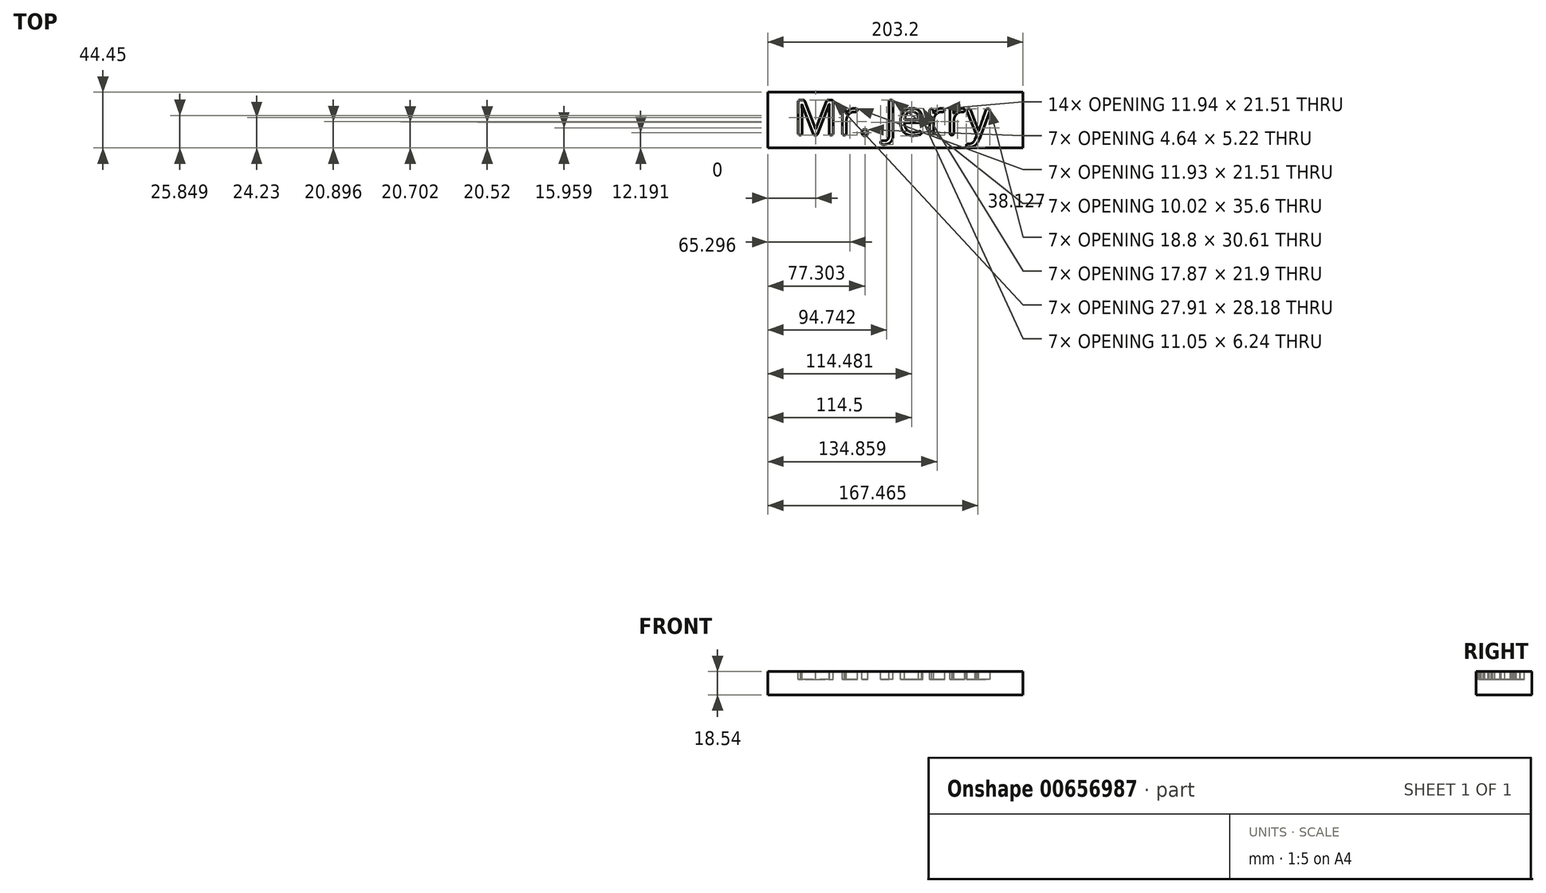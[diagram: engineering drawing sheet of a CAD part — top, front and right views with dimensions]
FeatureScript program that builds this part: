
annotation { "Feature Type Name" : "Feature", "Feature Type Description" : "" }
export const myFeature = defineFeature(function(context is Context, id is Id, definition is map)
    precondition{}
    {
        {
            var Q0;
            Q0=qCreatedBy(makeId("Top.planeOp"),FACE);
            var sketch = newSketch(context, id + "F0", { "sketchPlane" : qUnion([Q0])});
            skLineSegment(sketch, "E0.bottom", {"start": v(0, 0) * mm, "end": v(203.2, 0) * mm});
            skLineSegment(sketch, "E0.top", {"start": v(0, 44.45) * mm, "end": v(203.2, 44.45) * mm});
            skLineSegment(sketch, "E0.left", {"start": v(0, 0) * mm, "end": v(0, 44.45) * mm});
            skLineSegment(sketch, "E0.right", {"start": v(203.2, 0) * mm, "end": v(203.2, 44.45) * mm});
            skSolve(sketch);
        }
        {
            var Q0;
            Q0=makeQuery(id+"F0.imprint","IMPRINT",FACE,{"disambiguationData":[TD([[makeQuery(id+"F0.imprint","IMPRINT",EDGE,{"derivedFrom":sQuery(id+"F0.wireOp",EDGE,"E0.bottom")}),1.0]])]});
            extrude(context, id + "F1", {"entities" : qUnion([Q0]), "depth" : 18.54 * mm, "offsetDistance" : 25.4 * mm});
        }
        {
            var Q0;
            Q0=makeQuery(id+"F1.opExtrude","CAP_FACE",FACE,{"disambiguationData":[OSD([sQuery(id+"F0.wireOp",EDGE,"E0.bottom"),sQuery(id+"F0.wireOp",EDGE,"E0.top"),sQuery(id+"F0.wireOp",EDGE,"E0.left"),sQuery(id+"F0.wireOp",EDGE,"E0.right")])],"isStart":false});
            var sketch = newSketch(context, id + "F2", { "sketchPlane" : qUnion([Q0])});
            skText(sketch, "E1", { "text": "Mr. Jerry", "fontName": "OpenSans-Regular.ttf"});
            const initialGuessF2  = {"E1": [0.0203, 0.01014, 1, 0, 0.02842]};
            skSetInitialGuess(sketch, initialGuessF2);
            skSolve(sketch);
        }
        {
            var Q0;
            Q0 = qSketchRegion(id + "F2", true);
            extrude(context, id + "F3", {"entities" : qUnion([Q0]), "operationType" : NewBodyOperationType.REMOVE, "oppositeDirection" : true, "depth" : 6.35 * mm, "offsetDistance" : 25.4 * mm});
        }
        {
            var Q0;
            Q0=makeQuery(id+"F3.boolean.opBoolean","COPY",EDGE,{"derivedFrom":makeQuery(id+"F3.opExtrude","SWEPT_EDGE",EDGE,{"disambiguationData":[OSD([sQuery(id+"F2.wireOp",EDGE,"E1.sketch_text.stroke-5"),sQuery(id+"F2.wireOp",EDGE,"E1.sketch_text.stroke-6")])]})});
            var Q1;
            Q1=makeQuery(id+"F3.boolean.opBoolean","COPY",EDGE,{"derivedFrom":makeQuery(id+"F3.opExtrude","SWEPT_EDGE",EDGE,{"disambiguationData":[OSD([sQuery(id+"F2.wireOp",EDGE,"E1.sketch_text.stroke-6"),sQuery(id+"F2.wireOp",EDGE,"E1.sketch_text.stroke-7")])]})});
            var Q2;
            Q2=makeQuery(id+"F3.boolean.opBoolean","COPY",EDGE,{"derivedFrom":makeQuery(id+"F3.opExtrude","SWEPT_EDGE",EDGE,{"disambiguationData":[OSD([sQuery(id+"F2.wireOp",EDGE,"E1.sketch_text.stroke-9"),sQuery(id+"F2.wireOp",EDGE,"E1.sketch_text.stroke-10")])]})});
            var Q3;
            Q3=makeQuery(id+"F3.boolean.opBoolean","COPY",EDGE,{"derivedFrom":makeQuery(id+"F3.opExtrude","SWEPT_EDGE",EDGE,{"disambiguationData":[OSD([sQuery(id+"F2.wireOp",EDGE,"E1.sketch_text.stroke-10"),sQuery(id+"F2.wireOp",EDGE,"E1.sketch_text.stroke-11")])]})});
            var Q4;
            Q4=makeQuery(id+"F3.boolean.opBoolean","COPY",EDGE,{"derivedFrom":makeQuery(id+"F3.opExtrude","SWEPT_EDGE",EDGE,{"disambiguationData":[OSD([sQuery(id+"F2.wireOp",EDGE,"E1.sketch_text.stroke-26"),sQuery(id+"F2.wireOp",EDGE,"E1.sketch_text.stroke-27")])]})});
            var Q5;
            Q5=makeQuery(id+"F3.boolean.opBoolean","COPY",EDGE,{"derivedFrom":makeQuery(id+"F3.opExtrude","SWEPT_EDGE",EDGE,{"disambiguationData":[OSD([sQuery(id+"F2.wireOp",EDGE,"E1.sketch_text.stroke-18"),sQuery(id+"F2.wireOp",EDGE,"E1.sketch_text.stroke-19")])]})});
            var Q6;
            Q6=makeQuery(id+"F3.boolean.opBoolean","COPY",EDGE,{"derivedFrom":makeQuery(id+"F3.opExtrude","SWEPT_EDGE",EDGE,{"disambiguationData":[OSD([sQuery(id+"F2.wireOp",EDGE,"E1.sketch_text.stroke-25"),sQuery(id+"F2.wireOp",EDGE,"E1.sketch_text.stroke-26")])]})});
            var Q7;
            Q7=makeQuery(id+"F3.boolean.opBoolean","COPY",EDGE,{"derivedFrom":makeQuery(id+"F3.opExtrude","SWEPT_EDGE",EDGE,{"disambiguationData":[OSD([sQuery(id+"F2.wireOp",EDGE,"E1.sketch_text.stroke-3"),sQuery(id+"F2.wireOp",EDGE,"E1.sketch_text.stroke-4")])]})});
            var Q8;
            Q8=makeQuery(id+"F3.boolean.opBoolean","COPY",EDGE,{"derivedFrom":makeQuery(id+"F3.opExtrude","SWEPT_EDGE",EDGE,{"disambiguationData":[OSD([sQuery(id+"F2.wireOp",EDGE,"E1.sketch_text.stroke-4"),sQuery(id+"F2.wireOp",EDGE,"E1.sketch_text.stroke-5")])]})});
            var Q9;
            Q9=makeQuery(id+"F3.boolean.opBoolean","COPY",EDGE,{"derivedFrom":makeQuery(id+"F3.opExtrude","SWEPT_EDGE",EDGE,{"disambiguationData":[OSD([sQuery(id+"F2.wireOp",EDGE,"E1.sketch_text.stroke-12"),sQuery(id+"F2.wireOp",EDGE,"E1.sketch_text.stroke-13")])]})});
            var Q10;
            Q10=makeQuery(id+"F3.boolean.opBoolean","COPY",EDGE,{"derivedFrom":makeQuery(id+"F3.opExtrude","SWEPT_EDGE",EDGE,{"disambiguationData":[OSD([sQuery(id+"F2.wireOp",EDGE,"E1.sketch_text.stroke-0"),sQuery(id+"F2.wireOp",EDGE,"E1.sketch_text.stroke-17")])]})});
            var Q11;
            Q11=makeQuery(id+"F3.boolean.opBoolean","COPY",EDGE,{"derivedFrom":makeQuery(id+"F3.opExtrude","SWEPT_EDGE",EDGE,{"disambiguationData":[OSD([sQuery(id+"F2.wireOp",EDGE,"E1.sketch_text.stroke-16"),sQuery(id+"F2.wireOp",EDGE,"E1.sketch_text.stroke-17")])]})});
            var Q12;
            Q12=makeQuery(id+"F3.boolean.opBoolean","COPY",EDGE,{"derivedFrom":makeQuery(id+"F3.opExtrude","SWEPT_EDGE",EDGE,{"disambiguationData":[OSD([sQuery(id+"F2.wireOp",EDGE,"E1.sketch_text.stroke-23"),sQuery(id+"F2.wireOp",EDGE,"E1.sketch_text.stroke-24")])]})});
            var Q13;
            Q13=makeQuery(id+"F3.boolean.opBoolean","COPY",EDGE,{"derivedFrom":makeQuery(id+"F3.opExtrude","SWEPT_EDGE",EDGE,{"disambiguationData":[OSD([sQuery(id+"F2.wireOp",EDGE,"E1.sketch_text.stroke-11"),sQuery(id+"F2.wireOp",EDGE,"E1.sketch_text.stroke-12")])]})});
            var Q14;
            Q14=makeQuery(id+"F3.boolean.opBoolean","COPY",EDGE,{"derivedFrom":makeQuery(id+"F3.opExtrude","SWEPT_EDGE",EDGE,{"disambiguationData":[OSD([sQuery(id+"F2.wireOp",EDGE,"E1.sketch_text.stroke-24"),sQuery(id+"F2.wireOp",EDGE,"E1.sketch_text.stroke-25")])]})});
            var Q15;
            Q15=makeQuery(id+"F3.boolean.opBoolean","COPY",EDGE,{"derivedFrom":makeQuery(id+"F3.opExtrude","SWEPT_EDGE",EDGE,{"disambiguationData":[OSD([sQuery(id+"F2.wireOp",EDGE,"E1.sketch_text.stroke-19"),sQuery(id+"F2.wireOp",EDGE,"E1.sketch_text.stroke-20")])]})});
            var Q16;
            Q16=makeQuery(id+"F3.boolean.opBoolean","COPY",EDGE,{"derivedFrom":makeQuery(id+"F3.opExtrude","SWEPT_EDGE",EDGE,{"disambiguationData":[OSD([sQuery(id+"F2.wireOp",EDGE,"E1.sketch_text.stroke-44"),sQuery(id+"F2.wireOp",EDGE,"E1.sketch_text.stroke-45")])]})});
            var Q17;
            Q17=makeQuery(id+"F3.boolean.opBoolean","COPY",EDGE,{"derivedFrom":makeQuery(id+"F3.opExtrude","SWEPT_EDGE",EDGE,{"disambiguationData":[OSD([sQuery(id+"F2.wireOp",EDGE,"E1.sketch_text.stroke-40"),sQuery(id+"F2.wireOp",EDGE,"E1.sketch_text.stroke-41")])]})});
            var Q18;
            Q18=makeQuery(id+"F3.boolean.opBoolean","COPY",EDGE,{"derivedFrom":makeQuery(id+"F3.opExtrude","SWEPT_EDGE",EDGE,{"disambiguationData":[OSD([sQuery(id+"F2.wireOp",EDGE,"E1.sketch_text.stroke-45"),sQuery(id+"F2.wireOp",EDGE,"E1.sketch_text.stroke-46")])]})});
            var Q19;
            Q19=makeQuery(id+"F3.boolean.opBoolean","COPY",EDGE,{"derivedFrom":makeQuery(id+"F3.opExtrude","SWEPT_EDGE",EDGE,{"disambiguationData":[OSD([sQuery(id+"F2.wireOp",EDGE,"E1.sketch_text.stroke-39"),sQuery(id+"F2.wireOp",EDGE,"E1.sketch_text.stroke-40")])]})});
            var Q20;
            Q20=makeQuery(id+"F3.boolean.opBoolean","COPY",EDGE,{"derivedFrom":makeQuery(id+"F3.opExtrude","SWEPT_EDGE",EDGE,{"disambiguationData":[OSD([sQuery(id+"F2.wireOp",EDGE,"E1.sketch_text.stroke-55"),sQuery(id+"F2.wireOp",EDGE,"E1.sketch_text.stroke-56")])]})});
            var Q21;
            Q21=makeQuery(id+"F3.boolean.opBoolean","COPY",EDGE,{"derivedFrom":makeQuery(id+"F3.opExtrude","SWEPT_EDGE",EDGE,{"disambiguationData":[OSD([sQuery(id+"F2.wireOp",EDGE,"E1.sketch_text.stroke-60"),sQuery(id+"F2.wireOp",EDGE,"E1.sketch_text.stroke-61")])]})});
            var Q22;
            Q22=makeQuery(id+"F3.boolean.opBoolean","COPY",EDGE,{"derivedFrom":makeQuery(id+"F3.opExtrude","SWEPT_EDGE",EDGE,{"disambiguationData":[OSD([sQuery(id+"F2.wireOp",EDGE,"E1.sketch_text.stroke-59"),sQuery(id+"F2.wireOp",EDGE,"E1.sketch_text.stroke-60")])]})});
            var Q23;
            Q23=makeQuery(id+"F3.boolean.opBoolean","COPY",EDGE,{"derivedFrom":makeQuery(id+"F3.opExtrude","SWEPT_EDGE",EDGE,{"disambiguationData":[OSD([sQuery(id+"F2.wireOp",EDGE,"E1.sketch_text.stroke-68"),sQuery(id+"F2.wireOp",EDGE,"E1.sketch_text.stroke-69")])]})});
            var Q24;
            Q24=makeQuery(id+"F3.boolean.opBoolean","COPY",EDGE,{"derivedFrom":makeQuery(id+"F3.opExtrude","SWEPT_EDGE",EDGE,{"disambiguationData":[OSD([sQuery(id+"F2.wireOp",EDGE,"E1.sketch_text.stroke-69"),sQuery(id+"F2.wireOp",EDGE,"E1.sketch_text.stroke-70")])]})});
            var Q25;
            Q25=makeQuery(id+"F3.boolean.opBoolean","COPY",EDGE,{"derivedFrom":makeQuery(id+"F3.opExtrude","SWEPT_EDGE",EDGE,{"disambiguationData":[OSD([sQuery(id+"F2.wireOp",EDGE,"E1.sketch_text.stroke-76"),sQuery(id+"F2.wireOp",EDGE,"E1.sketch_text.stroke-77")])]})});
            var Q26;
            Q26=makeQuery(id+"F3.boolean.opBoolean","COPY",EDGE,{"derivedFrom":makeQuery(id+"F3.opExtrude","SWEPT_EDGE",EDGE,{"disambiguationData":[OSD([sQuery(id+"F2.wireOp",EDGE,"E1.sketch_text.stroke-75"),sQuery(id+"F2.wireOp",EDGE,"E1.sketch_text.stroke-76")])]})});
            var Q27;
            Q27=makeQuery(id+"F3.boolean.opBoolean","COPY",EDGE,{"derivedFrom":makeQuery(id+"F3.opExtrude","SWEPT_EDGE",EDGE,{"disambiguationData":[OSD([sQuery(id+"F2.wireOp",EDGE,"E1.sketch_text.stroke-74"),sQuery(id+"F2.wireOp",EDGE,"E1.sketch_text.stroke-75")])]})});
            var Q28;
            Q28=makeQuery(id+"F3.boolean.opBoolean","COPY",EDGE,{"derivedFrom":makeQuery(id+"F3.opExtrude","SWEPT_EDGE",EDGE,{"disambiguationData":[OSD([sQuery(id+"F2.wireOp",EDGE,"E1.sketch_text.stroke-73"),sQuery(id+"F2.wireOp",EDGE,"E1.sketch_text.stroke-74")])]})});
            var Q29;
            Q29=makeQuery(id+"F3.boolean.opBoolean","COPY",EDGE,{"derivedFrom":makeQuery(id+"F3.opExtrude","SWEPT_EDGE",EDGE,{"disambiguationData":[OSD([sQuery(id+"F2.wireOp",EDGE,"E1.sketch_text.stroke-88"),sQuery(id+"F2.wireOp",EDGE,"E1.sketch_text.stroke-89")])]})});
            var Q30;
            Q30=makeQuery(id+"F3.boolean.opBoolean","COPY",EDGE,{"derivedFrom":makeQuery(id+"F3.opExtrude","SWEPT_EDGE",EDGE,{"disambiguationData":[OSD([sQuery(id+"F2.wireOp",EDGE,"E1.sketch_text.stroke-89"),sQuery(id+"F2.wireOp",EDGE,"E1.sketch_text.stroke-90")])]})});
            var Q31;
            Q31=makeQuery(id+"F3.boolean.opBoolean","COPY",EDGE,{"derivedFrom":makeQuery(id+"F3.opExtrude","SWEPT_EDGE",EDGE,{"disambiguationData":[OSD([sQuery(id+"F2.wireOp",EDGE,"E1.sketch_text.stroke-81"),sQuery(id+"F2.wireOp",EDGE,"E1.sketch_text.stroke-82")])]})});
            var Q32;
            Q32=makeQuery(id+"F3.boolean.opBoolean","COPY",EDGE,{"derivedFrom":makeQuery(id+"F3.opExtrude","SWEPT_EDGE",EDGE,{"disambiguationData":[OSD([sQuery(id+"F2.wireOp",EDGE,"E1.sketch_text.stroke-82"),sQuery(id+"F2.wireOp",EDGE,"E1.sketch_text.stroke-83")])]})});
            var Q33;
            Q33=makeQuery(id+"F3.boolean.opBoolean","COPY",EDGE,{"derivedFrom":makeQuery(id+"F3.opExtrude","SWEPT_EDGE",EDGE,{"disambiguationData":[OSD([sQuery(id+"F2.wireOp",EDGE,"E1.sketch_text.stroke-87"),sQuery(id+"F2.wireOp",EDGE,"E1.sketch_text.stroke-88")])]})});
            var Q34;
            Q34=makeQuery(id+"F3.boolean.opBoolean","COPY",EDGE,{"derivedFrom":makeQuery(id+"F3.opExtrude","SWEPT_EDGE",EDGE,{"disambiguationData":[OSD([sQuery(id+"F2.wireOp",EDGE,"E1.sketch_text.stroke-86"),sQuery(id+"F2.wireOp",EDGE,"E1.sketch_text.stroke-87")])]})});
            var Q35;
            Q35=makeQuery(id+"F3.boolean.opBoolean","COPY",EDGE,{"derivedFrom":makeQuery(id+"F3.opExtrude","SWEPT_EDGE",EDGE,{"disambiguationData":[OSD([sQuery(id+"F2.wireOp",EDGE,"E1.sketch_text.stroke-94"),sQuery(id+"F2.wireOp",EDGE,"E1.sketch_text.stroke-95")])]})});
            var Q36;
            Q36=makeQuery(id+"F3.boolean.opBoolean","COPY",EDGE,{"derivedFrom":makeQuery(id+"F3.opExtrude","SWEPT_EDGE",EDGE,{"disambiguationData":[OSD([sQuery(id+"F2.wireOp",EDGE,"E1.sketch_text.stroke-99"),sQuery(id+"F2.wireOp",EDGE,"E1.sketch_text.stroke-100")])]})});
            var Q37;
            Q37=makeQuery(id+"F3.boolean.opBoolean","COPY",EDGE,{"derivedFrom":makeQuery(id+"F3.opExtrude","SWEPT_EDGE",EDGE,{"disambiguationData":[OSD([sQuery(id+"F2.wireOp",EDGE,"E1.sketch_text.stroke-94"),sQuery(id+"F2.wireOp",EDGE,"E1.sketch_text.stroke-109")])]})});
            var Q38;
            Q38=makeQuery(id+"F3.boolean.opBoolean","COPY",EDGE,{"derivedFrom":makeQuery(id+"F3.opExtrude","SWEPT_EDGE",EDGE,{"disambiguationData":[OSD([sQuery(id+"F2.wireOp",EDGE,"E1.sketch_text.stroke-100"),sQuery(id+"F2.wireOp",EDGE,"E1.sketch_text.stroke-101")])]})});
            var Q39;
            Q39=makeQuery(id+"F3.boolean.opBoolean","COPY",EDGE,{"derivedFrom":makeQuery(id+"F3.opExtrude","SWEPT_EDGE",EDGE,{"disambiguationData":[OSD([sQuery(id+"F2.wireOp",EDGE,"E1.sketch_text.stroke-105"),sQuery(id+"F2.wireOp",EDGE,"E1.sketch_text.stroke-106")])]})});
            var Q40;
            Q40=makeQuery(id+"F3.boolean.opBoolean","COPY",EDGE,{"derivedFrom":makeQuery(id+"F3.opExtrude","SWEPT_EDGE",EDGE,{"disambiguationData":[OSD([sQuery(id+"F2.wireOp",EDGE,"E1.sketch_text.stroke-104"),sQuery(id+"F2.wireOp",EDGE,"E1.sketch_text.stroke-105")])]})});
            fillet(context, id + "F4", {"entities" : qUnion([Q0, Q1, Q2, Q3, Q4, Q5, Q6, Q7, Q8, Q9, Q10, Q11, Q12, Q13, Q14, Q15, Q16, Q17, Q18, Q19, Q20, Q21, Q22, Q23, Q24, Q25, Q26, Q27, Q28, Q29, Q30, Q31, Q32, Q33, Q34, Q35, Q36, Q37, Q38, Q39, Q40]), "radius" : 1.59 * mm, "tangentPropagation" : true, "allowEdgeOverflow" : false});
        }
    });
